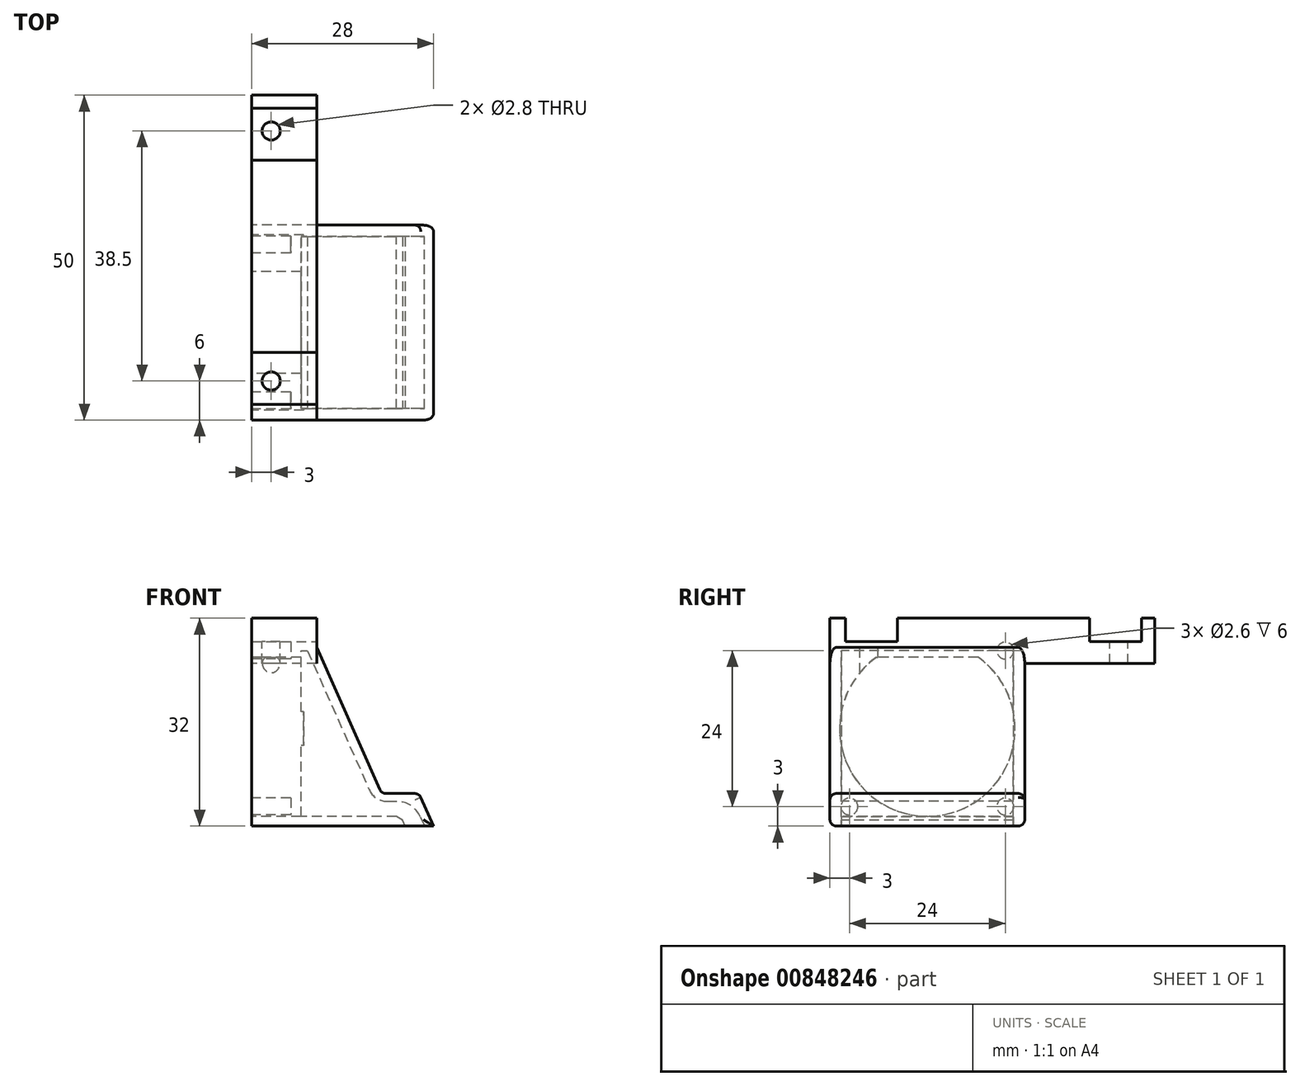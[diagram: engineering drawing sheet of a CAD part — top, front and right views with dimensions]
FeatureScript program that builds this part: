
annotation { "Feature Type Name" : "Feature", "Feature Type Description" : "" }
export const myFeature = defineFeature(function(context is Context, id is Id, definition is map)
    precondition{}
    {
        {
            var Q0;
            Q0=qCreatedBy(makeId("Front.planeOp"),FACE);
            var sketch = newSketch(context, id + "F0", { "sketchPlane" : qUnion([Q0])});
            skLineSegment(sketch, "E0", {"start": v(0, 0) * mm, "end": v(0, 32) * mm});
            skLineSegment(sketch, "E1", {"start": v(0, 32) * mm, "end": v(8, 32) * mm});
            skLineSegment(sketch, "E2", {"start": v(8, 32) * mm, "end": v(20, 5) * mm});
            skLineSegment(sketch, "E3", {"start": v(28, 0) * mm, "end": v(0, 0) * mm});
            skLineSegment(sketch, "E4", {"start": v(20, 5) * mm, "end": v(25.78, 5) * mm});
            skLineSegment(sketch, "E5", {"start": v(25.78, 5) * mm, "end": v(28, 0) * mm});
            skSolve(sketch);
        }
        {
            var Q0;
            Q0=makeQuery(id+"F0.imprint","IMPRINT",FACE,{"disambiguationData":[TD([[makeQuery(id+"F0.imprint","IMPRINT",EDGE,{"derivedFrom":sQuery(id+"F0.wireOp",EDGE,"E0")}),-1.0]])]});
            extrude(context, id + "F1", {"entities" : qUnion([Q0]), "depth" : 30 * mm, "offsetDistance" : 25 * mm});
        }
        {
            var Q0;
            Q0=makeQuery(id+"F1.opExtrude","SWEPT_FACE",FACE,{"disambiguationData":[OSD([sQuery(id+"F0.wireOp",EDGE,"E1")])]});
            var sketch = newSketch(context, id + "F2", { "sketchPlane" : qUnion([Q0])});
            skLineSegment(sketch, "E6.bottom", {"start": v(0, -30) * mm, "end": v(10, -30) * mm});
            skLineSegment(sketch, "E6.top", {"start": v(0, 20) * mm, "end": v(10, 20) * mm});
            skLineSegment(sketch, "E6.left", {"start": v(0, -30) * mm, "end": v(0, 20) * mm});
            skLineSegment(sketch, "E6.right", {"start": v(10, -30) * mm, "end": v(10, 20) * mm});
            skSolve(sketch);
        }
        {
            var Q0;
            Q0=qSketchRegion(id+"F2",true);
            extrude(context, id + "F3", {"entities" : qUnion([Q0]), "operationType" : NewBodyOperationType.ADD, "oppositeDirection" : true, "depth" : 7 * mm, "offsetDistance" : 25 * mm});
        }
        {
            var Q0;
            Q0=makeQuery(id+"F3.boolean.opBoolean","MERGE",FACE,{"derivedFrom":[makeQuery(id+"F1.opExtrude","SWEPT_FACE",FACE,{"disambiguationData":[OSD([sQuery(id+"F0.wireOp",EDGE,"E1")])]}),makeQuery(id+"F3.opExtrude","CAP_FACE",FACE,{"disambiguationData":[OSD([sQuery(id+"F2.wireOp",EDGE,"E6.bottom"),sQuery(id+"F2.wireOp",EDGE,"E6.top"),sQuery(id+"F2.wireOp",EDGE,"E6.left"),sQuery(id+"F2.wireOp",EDGE,"E6.right")])],"isStart":true})]});
            var sketch = newSketch(context, id + "F4", { "sketchPlane" : qUnion([Q0])});
            skLineSegment(sketch, "E7.bottom", {"start": v(0, 18) * mm, "end": v(10, 18) * mm});
            skLineSegment(sketch, "E7.top", {"start": v(0, 10) * mm, "end": v(10, 10) * mm});
            skLineSegment(sketch, "E7.left", {"start": v(0, 18) * mm, "end": v(0, 10) * mm});
            skLineSegment(sketch, "E7.right", {"start": v(10, 18) * mm, "end": v(10, 10) * mm});
            skLineSegment(sketch, "E8.bottom", {"start": v(0, -19.6) * mm, "end": v(12, -19.6) * mm});
            skLineSegment(sketch, "E8.top", {"start": v(0, -27.6) * mm, "end": v(12, -27.6) * mm});
            skLineSegment(sketch, "E8.left", {"start": v(0, -19.6) * mm, "end": v(0, -27.6) * mm});
            skLineSegment(sketch, "E8.right", {"start": v(12, -19.6) * mm, "end": v(12, -27.6) * mm});
            skSolve(sketch);
        }
        {
            var Q0;
            Q0=makeQuery(id+"F4.imprint","IMPRINT",FACE,{"disambiguationData":[TD([[makeQuery(id+"F4.imprint","IMPRINT",EDGE,{"derivedFrom":sQuery(id+"F4.wireOp",EDGE,"E7.bottom")}),-1.0]])]});
            var Q1;
            Q1=makeQuery(id+"F4.imprint","IMPRINT",FACE,{"disambiguationData":[TD([[makeQuery(id+"F4.imprint","IMPRINT",EDGE,{"derivedFrom":sQuery(id+"F4.wireOp",EDGE,"E8.bottom")}),-1.0]])]});
            extrude(context, id + "F5", {"entities" : qUnion([Q0, Q1]), "operationType" : NewBodyOperationType.REMOVE, "oppositeDirection" : true, "depth" : 3.6 * mm, "offsetDistance" : 25 * mm});
        }
        {
            var Q0;
            Q0=qCreatedBy(makeId("Front.planeOp"),FACE);
            cPlane(context, id + "F6", {"entities" : qUnion([Q0]), "cplaneType" : CPlaneType.OFFSET, "offset" : 28.25 * mm, "width" : 150 * mm, "height" : 150 * mm});
        }
        {
            var Q0;
            Q0=qCreatedBy(id+"F6.planeOp",FACE);
            var sketch = newSketch(context, id + "F7", { "sketchPlane" : qUnion([Q0])});
            skLineSegment(sketch, "E9", {"start": v(8.58, 27) * mm, "end": v(18.9, 3.8) * mm});
            skLineSegment(sketch, "E10", {"start": v(27.5, -2) * mm, "end": v(24.5, -2) * mm});
            skLineSegment(sketch, "E11", {"start": v(24.5, -2) * mm, "end": v(22.94, 1.5) * mm});
            skLineSegment(sketch, "E12", {"start": v(22.94, 1.5) * mm, "end": v(7.58, 1.5) * mm});
            skLineSegment(sketch, "E13", {"start": v(7.58, 1.5) * mm, "end": v(7.58, 27) * mm});
            skLineSegment(sketch, "E14", {"start": v(7.58, 27) * mm, "end": v(8.58, 27) * mm});
            skLineSegment(sketch, "E15", {"start": v(18.9, 3.8) * mm, "end": v(24.92, 3.8) * mm});
            skLineSegment(sketch, "E16", {"start": v(24.92, 3.8) * mm, "end": v(27.5, -2) * mm});
            skSolve(sketch);
        }
        {
            var Q0;
            Q0=qSketchRegion(id+"F7",true);
            extrude(context, id + "F8", {"entities" : qUnion([Q0]), "operationType" : NewBodyOperationType.REMOVE, "oppositeDirection" : true, "depth" : 26.5 * mm, "offsetDistance" : 25 * mm});
        }
        {
            var Q0;
            Q0=makeQuery(id+"F3.boolean.opBoolean","MERGE",FACE,{"derivedFrom":[makeQuery(id+"F1.opExtrude","SWEPT_FACE",FACE,{"disambiguationData":[OSD([sQuery(id+"F0.wireOp",EDGE,"E0")])]}),makeQuery(id+"F3.opExtrude","SWEPT_FACE",FACE,{"disambiguationData":[OSD([sQuery(id+"F2.wireOp",EDGE,"E6.left")])]})]});
            var sketch = newSketch(context, id + "F9", { "sketchPlane" : qUnion([Q0])});
            skArc(sketch, "E17", {"start": v(7.17, 26) * mm, "mid": v(15, 1.5) * mm, "end": v(22.83, 26) * mm});
            skLineSegment(sketch, "E18", {"start": v(7.17, 26) * mm, "end": v(22.83, 26) * mm});
            skSolve(sketch);
        }
        {
            var Q0;
            Q0=makeQuery(id+"F9.imprint","IMPRINT",FACE,{"disambiguationData":[TD([[makeQuery(id+"F9.imprint","IMPRINT",EDGE,{"derivedFrom":sQuery(id+"F9.wireOp",EDGE,"E17")}),1.0]])]});
            extrude(context, id + "F10", {"entities" : qUnion([Q0]), "operationType" : NewBodyOperationType.REMOVE, "oppositeDirection" : true, "depth" : 8 * mm, "offsetDistance" : 25 * mm});
        }
        {
            var Q0;
            Q0=makeQuery(id+"F3.boolean.opBoolean","MERGE",FACE,{"derivedFrom":[makeQuery(id+"F1.opExtrude","SWEPT_FACE",FACE,{"disambiguationData":[OSD([sQuery(id+"F0.wireOp",EDGE,"E0")])]}),makeQuery(id+"F3.opExtrude","SWEPT_FACE",FACE,{"disambiguationData":[OSD([sQuery(id+"F2.wireOp",EDGE,"E6.left")])]})]});
            var sketch = newSketch(context, id + "F11", { "sketchPlane" : qUnion([Q0])});
            skCircle(sketch, "E19", {"center": v(3, 27) * mm, "radius": 1.3 * mm});
            skCircle(sketch, "E20", {"center": v(3, 3) * mm, "radius": 1.3 * mm});
            skCircle(sketch, "E21", {"center": v(27, 3) * mm, "radius": 1.3 * mm});
            skSolve(sketch);
        }
        {
            var Q0;
            Q0=qSketchRegion(id+"F11",true);
            extrude(context, id + "F12", {"entities" : qUnion([Q0]), "operationType" : NewBodyOperationType.REMOVE, "oppositeDirection" : true, "depth" : 6 * mm, "offsetDistance" : 25 * mm});
        }
        {
            var Q0;
            Q0=makeQuery(id+"F1.opExtrude","CAP_EDGE",EDGE,{"disambiguationData":[OSD([sQuery(id+"F0.wireOp",EDGE,"E2")])],"isStart":false});
            var Q1;
            Q1=makeQuery(id+"F1.opExtrude","CAP_EDGE",EDGE,{"disambiguationData":[OSD([sQuery(id+"F0.wireOp",EDGE,"E2")])],"isStart":true});
            var Q2;
            Q2=makeQuery(id+"F1.opExtrude","CAP_EDGE",EDGE,{"disambiguationData":[OSD([sQuery(id+"F0.wireOp",EDGE,"E5")])],"isStart":false});
            var Q3;
            Q3=makeQuery(id+"F1.opExtrude","CAP_EDGE",EDGE,{"disambiguationData":[OSD([sQuery(id+"F0.wireOp",EDGE,"E4")])],"isStart":false});
            var Q4;
            Q4=makeQuery(id+"F1.opExtrude","CAP_EDGE",EDGE,{"disambiguationData":[OSD([sQuery(id+"F0.wireOp",EDGE,"E5")])],"isStart":true});
            var Q5;
            Q5=makeQuery(id+"F1.opExtrude","CAP_EDGE",EDGE,{"disambiguationData":[OSD([sQuery(id+"F0.wireOp",EDGE,"E4")])],"isStart":true});
            var Q6;
            Q6=makeQuery(id+"F1.opExtrude","SWEPT_EDGE",EDGE,{"disambiguationData":[OSD([sQuery(id+"F0.wireOp",EDGE,"E4"),sQuery(id+"F0.wireOp",EDGE,"E5")])]});
            var Q7;
            Q7=makeQuery(id+"F1.opExtrude","SWEPT_EDGE",EDGE,{"disambiguationData":[OSD([sQuery(id+"F0.wireOp",EDGE,"E2"),sQuery(id+"F0.wireOp",EDGE,"E4")])]});
            var Q8;
            Q8=makeQuery(id+"F1.opExtrude","CAP_EDGE",EDGE,{"disambiguationData":[OSD([sQuery(id+"F0.wireOp",EDGE,"E3")])],"isStart":false});
            var Q9;
            Q9=makeQuery(id+"F1.opExtrude","CAP_EDGE",EDGE,{"disambiguationData":[OSD([sQuery(id+"F0.wireOp",EDGE,"E3")])],"isStart":true});
            fillet(context, id + "F13", {"entities" : qUnion([Q0, Q1, Q2, Q3, Q4, Q5, Q6, Q7, Q8, Q9]), "radius" : 1 * mm, "tangentPropagation" : true, "allowEdgeOverflow" : false});
        }
        {
            var Q0;
            Q0=makeQuery(id+"F5.boolean.opBoolean","COPY",FACE,{"derivedFrom":makeQuery(id+"F5.opExtrude","CAP_FACE",FACE,{"disambiguationData":[OSD([sQuery(id+"F4.wireOp",EDGE,"E7.bottom"),sQuery(id+"F4.wireOp",EDGE,"E7.top"),sQuery(id+"F4.wireOp",EDGE,"E7.left"),sQuery(id+"F4.wireOp",EDGE,"E7.right")])],"isStart":false})});
            var sketch = newSketch(context, id + "F14", { "sketchPlane" : qUnion([Q0])});
            skCircle(sketch, "E22", {"center": v(3, 14.5) * mm, "radius": 1.4 * mm});
            skSolve(sketch);
        }
        {
            var Q0;
            Q0=makeQuery(id+"F5.boolean.opBoolean","COPY",FACE,{"derivedFrom":makeQuery(id+"F5.opExtrude","CAP_FACE",FACE,{"disambiguationData":[OSD([sQuery(id+"F4.wireOp",EDGE,"E8.bottom"),sQuery(id+"F4.wireOp",EDGE,"E8.top"),sQuery(id+"F4.wireOp",EDGE,"E8.left"),sQuery(id+"F4.wireOp",EDGE,"E8.right")])],"isStart":false})});
            var sketch = newSketch(context, id + "F15", { "sketchPlane" : qUnion([Q0])});
            skCircle(sketch, "E23", {"center": v(3, -24) * mm, "radius": 1.4 * mm});
            skSolve(sketch);
        }
        {
            var Q0;
            Q0=qSketchRegion(id+"F14",true);
            extrude(context, id + "F16", {"entities" : qUnion([Q0]), "operationType" : NewBodyOperationType.REMOVE, "oppositeDirection" : true, "depth" : 5 * mm, "offsetDistance" : 25 * mm});
        }
        {
            var Q0;
            Q0=qSketchRegion(id+"F15",true);
            extrude(context, id + "F17", {"entities" : qUnion([Q0]), "operationType" : NewBodyOperationType.REMOVE, "oppositeDirection" : true, "depth" : 5 * mm, "offsetDistance" : 25 * mm});
        }
        {
            var Q0;
            Q0=makeQuery(id+"F8.boolean.opBoolean","COPY",EDGE,{"derivedFrom":makeQuery(id+"F8.opExtrude","SWEPT_EDGE",EDGE,{"disambiguationData":[OSD([sQuery(id+"F7.wireOp",EDGE,"E9"),sQuery(id+"F7.wireOp",EDGE,"E15")])]})});
            fillet(context, id + "F18", {"entities" : qUnion([Q0]), "radius" : 3 * mm, "tangentPropagation" : true, "allowEdgeOverflow" : false});
        }
        {
            var Q0;
            Q0=makeQuery(id+"F8.boolean.opBoolean","COPY",EDGE,{"derivedFrom":makeQuery(id+"F8.opExtrude","SWEPT_EDGE",EDGE,{"disambiguationData":[OSD([sQuery(id+"F7.wireOp",EDGE,"E15"),sQuery(id+"F7.wireOp",EDGE,"E16")])]})});
            fillet(context, id + "F19", {"entities" : qUnion([Q0]), "radius" : 4 * mm, "tangentPropagation" : true, "allowEdgeOverflow" : false});
        }
        {
            var Q0;
            Q0=makeQuery(id+"F8.boolean.opBoolean","COPY",EDGE,{"derivedFrom":makeQuery(id+"F8.opExtrude","SWEPT_EDGE",EDGE,{"disambiguationData":[OSD([sQuery(id+"F7.wireOp",EDGE,"E11"),sQuery(id+"F7.wireOp",EDGE,"E12")])]})});
            chamfer(context, id + "F20", {"entities" : qUnion([Q0]), "width" : 1 * mm, "tangentPropagation" : true});
        }
    });
